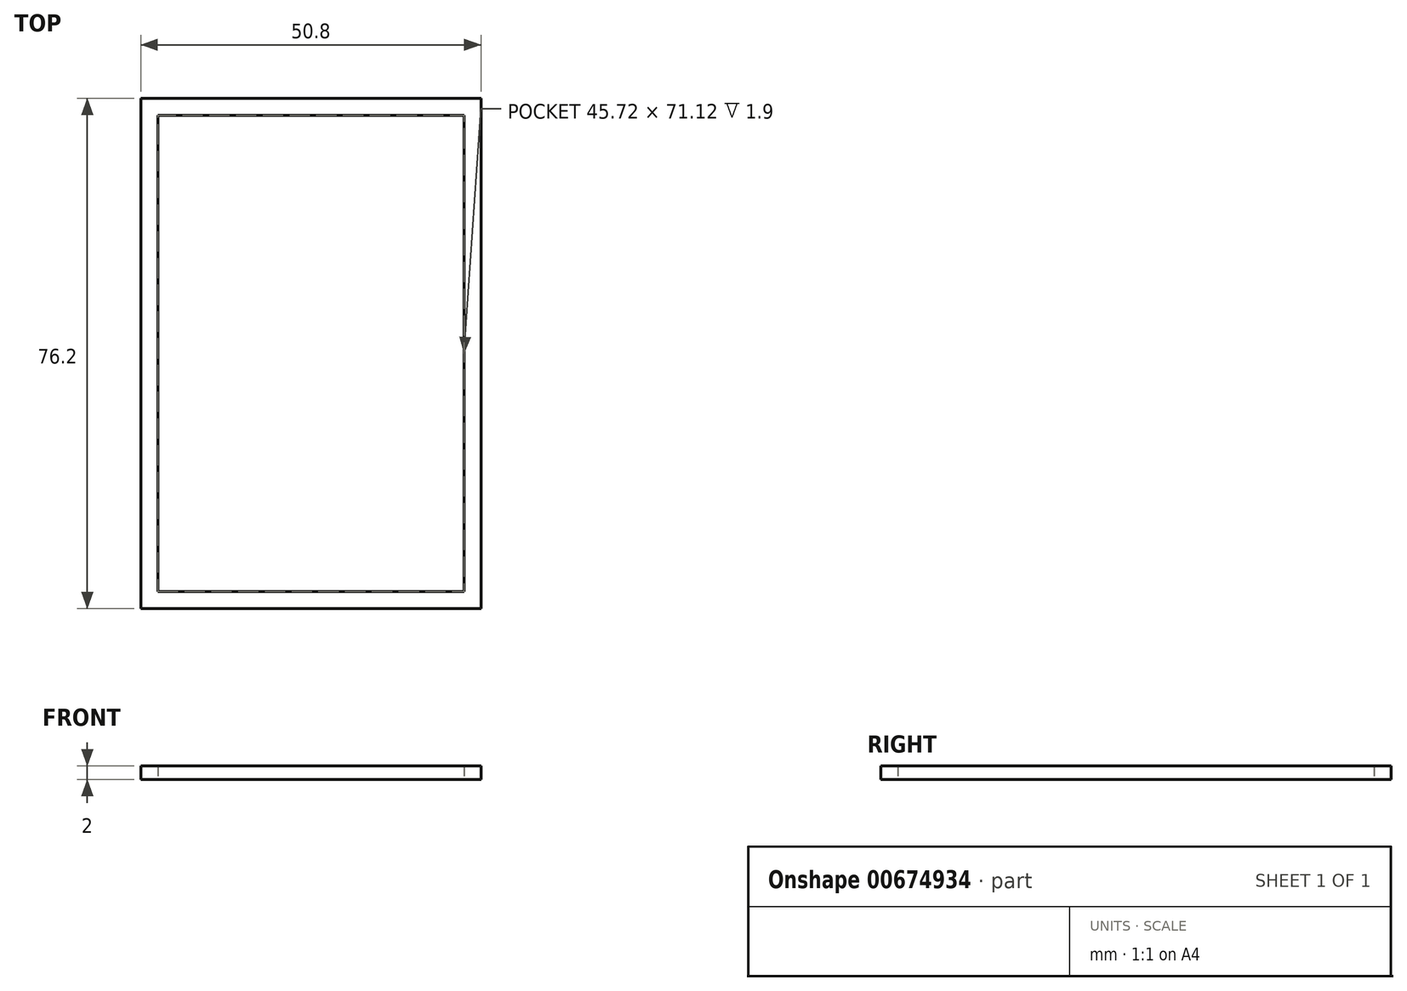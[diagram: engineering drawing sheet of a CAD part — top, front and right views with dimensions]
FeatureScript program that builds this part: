
annotation { "Feature Type Name" : "Feature", "Feature Type Description" : "" }
export const myFeature = defineFeature(function(context is Context, id is Id, definition is map)
    precondition{}
    {
        {
            assignVariable(context, id + "F0", {"name" : "depth", "anyValue" : 2});
        }
        {
            assignVariable(context, id + "F1", {"name" : "thickness", "anyValue" : .1});
        }
        {
            var Q0;
            Q0=qCreatedBy(makeId("Top.planeOp"),FACE);
            var sketch = newSketch(context, id + "F2", { "sketchPlane" : qUnion([Q0])});
            skLineSegment(sketch, "E0.bottom", {"start": v(0, 0) * mm, "end": v(50.8, 0) * mm});
            skLineSegment(sketch, "E0.top", {"start": v(0, 76.2) * mm, "end": v(50.8, 76.2) * mm});
            skLineSegment(sketch, "E0.left", {"start": v(0, 0) * mm, "end": v(0, 76.2) * mm});
            skLineSegment(sketch, "E0.right", {"start": v(50.8, 0) * mm, "end": v(50.8, 76.2) * mm});
            skLineSegment(sketch, "E1.0", {"start": v(2.54, 2.54) * mm, "end": v(2.54, 73.66) * mm});
            skLineSegment(sketch, "E1.1", {"start": v(2.54, 2.54) * mm, "end": v(48.26, 2.54) * mm});
            skLineSegment(sketch, "E1.2", {"start": v(48.26, 2.54) * mm, "end": v(48.26, 73.66) * mm});
            skLineSegment(sketch, "E1.3", {"start": v(2.54, 73.66) * mm, "end": v(48.26, 73.66) * mm});
            skSolve(sketch);
        }
        {
            var Q0;
            Q0 = qSketchRegion(id + "F2", true);
            extrude(context, id + "F3", {"entities" : qUnion([Q0]), "depth" : (getVariable(context, 'depth')) * mm, "offsetDistance" : 25.4 * mm});
        }
        {
            var Q0;
            Q0=qCreatedBy(makeId("Top.planeOp"),FACE);
            var sketch = newSketch(context, id + "F4", { "sketchPlane" : qUnion([Q0])});
            skLineSegment(sketch, "E2.bottom", {"start": v(0, 0) * mm, "end": v(50.8, 0) * mm});
            skLineSegment(sketch, "E2.top", {"start": v(0, 76.2) * mm, "end": v(50.8, 76.2) * mm});
            skLineSegment(sketch, "E2.left", {"start": v(0, 0) * mm, "end": v(0, 76.2) * mm});
            skLineSegment(sketch, "E2.right", {"start": v(50.8, 0) * mm, "end": v(50.8, 76.2) * mm});
            skSolve(sketch);
        }
        {
            var Q0;
            Q0 = qSketchRegion(id + "F4", true);
            extrude(context, id + "F5", {"entities" : qUnion([Q0]), "operationType" : NewBodyOperationType.ADD, "depth" : (getVariable(context, 'thickness')) * mm, "offsetDistance" : 25.4 * mm});
        }
        {
            assignVariable(context, id + "F6", {"name" : "inputd", "anyValue" : .5});
        }
        {
            var Q0;
            Q0=makeQuery(id+"F3.opExtrude","SWEPT_FACE",FACE,{"disambiguationData":[OSD([sQuery(id+"F2.wireOp",EDGE,"E0.left")])]});
            var sketch = newSketch(context, id + "F7", { "sketchPlane" : qUnion([Q0])});
            skLineSegment(sketch, "E3", {"start": v(0, 10.57) * mm, "end": v(-76.2, 10.57) * mm, "construction": true});
            skPoint(sketch, "E4", {"position": v(-14.49, 10.57) * mm});
            skPoint(sketch, "E5", {"position": v(-32.96, 10.57) * mm});
            skPoint(sketch, "E6", {"position": v(-45.48, 10.57) * mm});
            skPoint(sketch, "E7", {"position": v(-63.6, 10.57) * mm});
            skSolve(sketch);
        }
        {
            var Q0;
            Q0=sQuery(id+"F7.wireOp",VERTEX,"E4");
            var Q1;
            Q1=sQuery(id+"F7.wireOp",VERTEX,"E5");
            var Q2;
            Q2=sQuery(id+"F7.wireOp",VERTEX,"E6");
            var Q3;
            Q3=sQuery(id+"F7.wireOp",VERTEX,"E7");
            var Q4;
            Q4=makeQuery(id+"F3.opExtrude","SWEPT_BODY",BODY,{"disambiguationData":[OSD([sQuery(id+"F2.wireOp",EDGE,"E0.bottom"),sQuery(id+"F2.wireOp",EDGE,"E0.top"),sQuery(id+"F2.wireOp",EDGE,"E0.left"),sQuery(id+"F2.wireOp",EDGE,"E0.right"),sQuery(id+"F2.wireOp",EDGE,"E1.0"),sQuery(id+"F2.wireOp",EDGE,"E1.1"),sQuery(id+"F2.wireOp",EDGE,"E1.2"),sQuery(id+"F2.wireOp",EDGE,"E1.3")])]});
            hole(context, id + "F8", {"style" : HoleStyle.SIMPLE, "endStyle" : HoleEndStyle.BLIND, "holeDiameter" : (getVariable(context, 'inputd')) * mm, "majorDiameter" : 6.35 * mm, "holeDepth" : 5.08 * mm, "isTappedThrough" : true, "tappedDepth" : 12.7 * mm, "tapClearance" : 3, "startFromSketch" : true, "locations" : qUnion([Q0, Q1, Q2, Q3]), "scope" : qUnion([Q4])});
        }
    });
